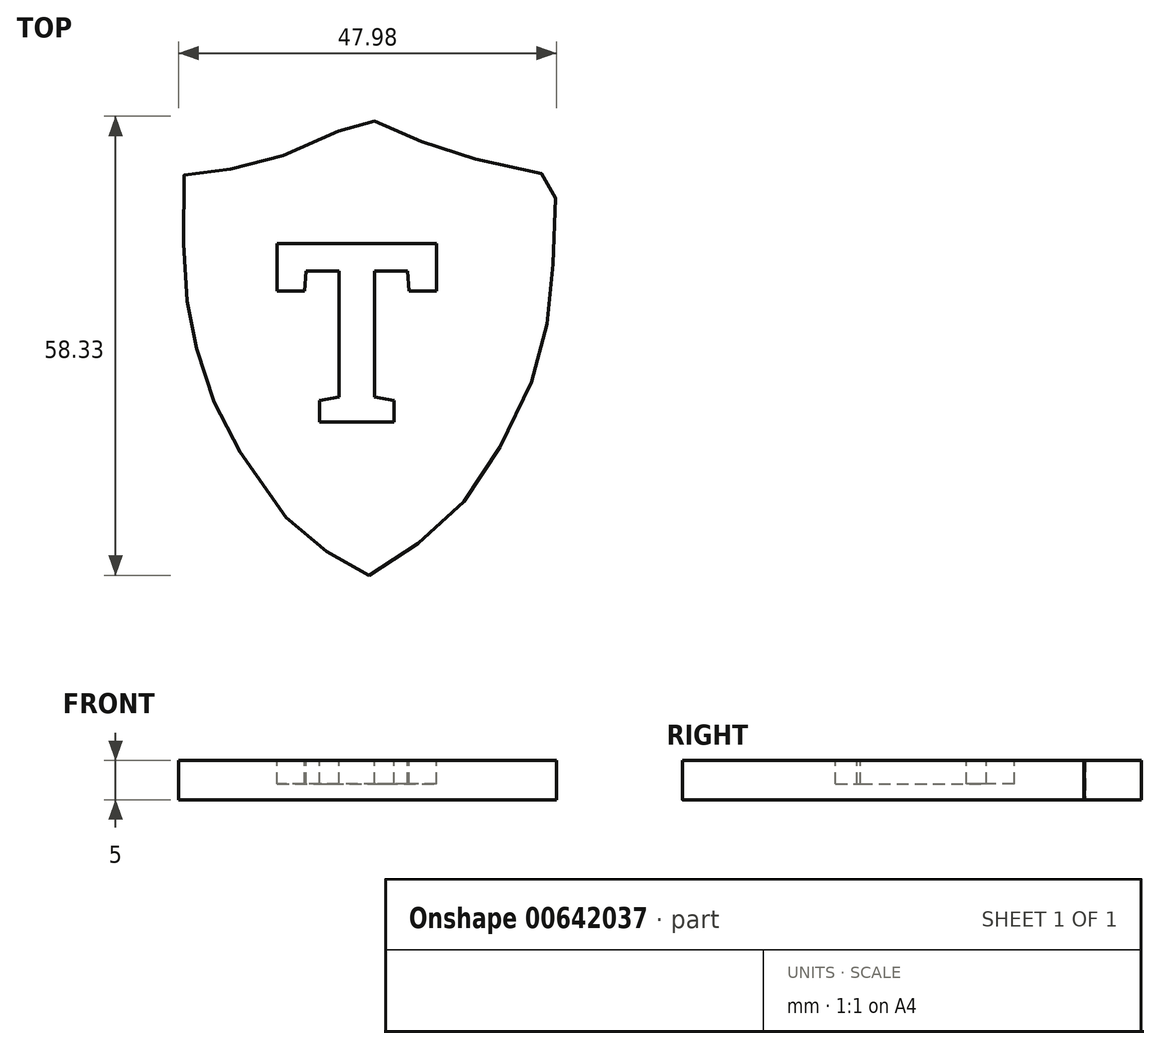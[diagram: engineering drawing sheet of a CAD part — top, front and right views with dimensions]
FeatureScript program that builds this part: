
annotation { "Feature Type Name" : "Feature", "Feature Type Description" : "" }
export const myFeature = defineFeature(function(context is Context, id is Id, definition is map)
    precondition{}
    {
        {
            var Q0;
            Q0=qCreatedBy(makeId("Top.planeOp"),FACE);
            var sketch = newSketch(context, id + "F0", { "sketchPlane" : qUnion([Q0])});
            skFitSpline(sketch, "E0", {"points": [v(1.68, -26.9) * mm, v(-2.01, -25.24) * mm, v(-5.47, -22.34) * mm, v(-9.87, -18.4) * mm, v(-16, -8.9) * mm, v(-17.97, -4.97) * mm, v(-19.7, 0) * mm, v(-21.03, 5.57) * mm, v(-21.43, 8.47) * mm, v(-21.74, 14.37) * mm, v(-22.05, 23.64) * mm, v(-19.3, 24.27) * mm, v(-14.35, 25.06) * mm, v(-9.4, 26.4) * mm, v(-4.06, 28.44) * mm, v(1.37, 31.42) * mm, v(1.92, 31.11) * mm, v(4.67, 29.77) * mm, v(9.7, 27.65) * mm, v(15.2, 26) * mm, v(23.37, 24.11) * mm, v(25.26, 24.04) * mm, v(25.42, 21.29) * mm, v(25.1, 13.66) * mm, v(24.63, 6.98) * mm, v(23.3, 0.93) * mm, v(20.94, -5.99) * mm, v(15.83, -14.48) * mm, v(12.37, -19.11) * mm, v(6.48, -23.99) * mm, v(1.68, -26.9) * mm]});
            skSolve(sketch);
        }
        {
            var Q0;
            Q0 = qSketchRegion(id + "F0", true);
            extrude(context, id + "F1", {"entities" : qUnion([Q0]), "depth" : 5 * mm, "offsetDistance" : 25 * mm});
        }
        {
            var Q0;
            Q0=makeQuery(id+"F1.opExtrude","CAP_FACE",FACE,{"disambiguationData":[OSD([sQuery(id+"F0.wireOp",EDGE,"E0")])],"isStart":false});
            var sketch = newSketch(context, id + "F2", { "sketchPlane" : qUnion([Q0])});
            skText(sketch, "E1", { "text": "T", "fontName": "RobotoSlab-Bold.ttf"});
            const initialGuessF2  = {"E1": [-0.01058, -0.00745, 1, 0, 0.023]};
            skSetInitialGuess(sketch, initialGuessF2);
            skSolve(sketch);
        }
        {
            var Q0;
            Q0=makeQuery(id+"F2.imprint","IMPRINT",FACE,{"disambiguationData":[TD([[makeQuery(id+"F2.imprint","IMPRINT",EDGE,{"derivedFrom":sQuery(id+"F2.wireOp",EDGE,"E1.sketch_text.stroke-0")}),-1.0]])]});
            extrude(context, id + "F3", {"entities" : qUnion([Q0]), "operationType" : NewBodyOperationType.REMOVE, "oppositeDirection" : true, "depth" : 3 * mm, "offsetDistance" : 25 * mm});
        }
    });
